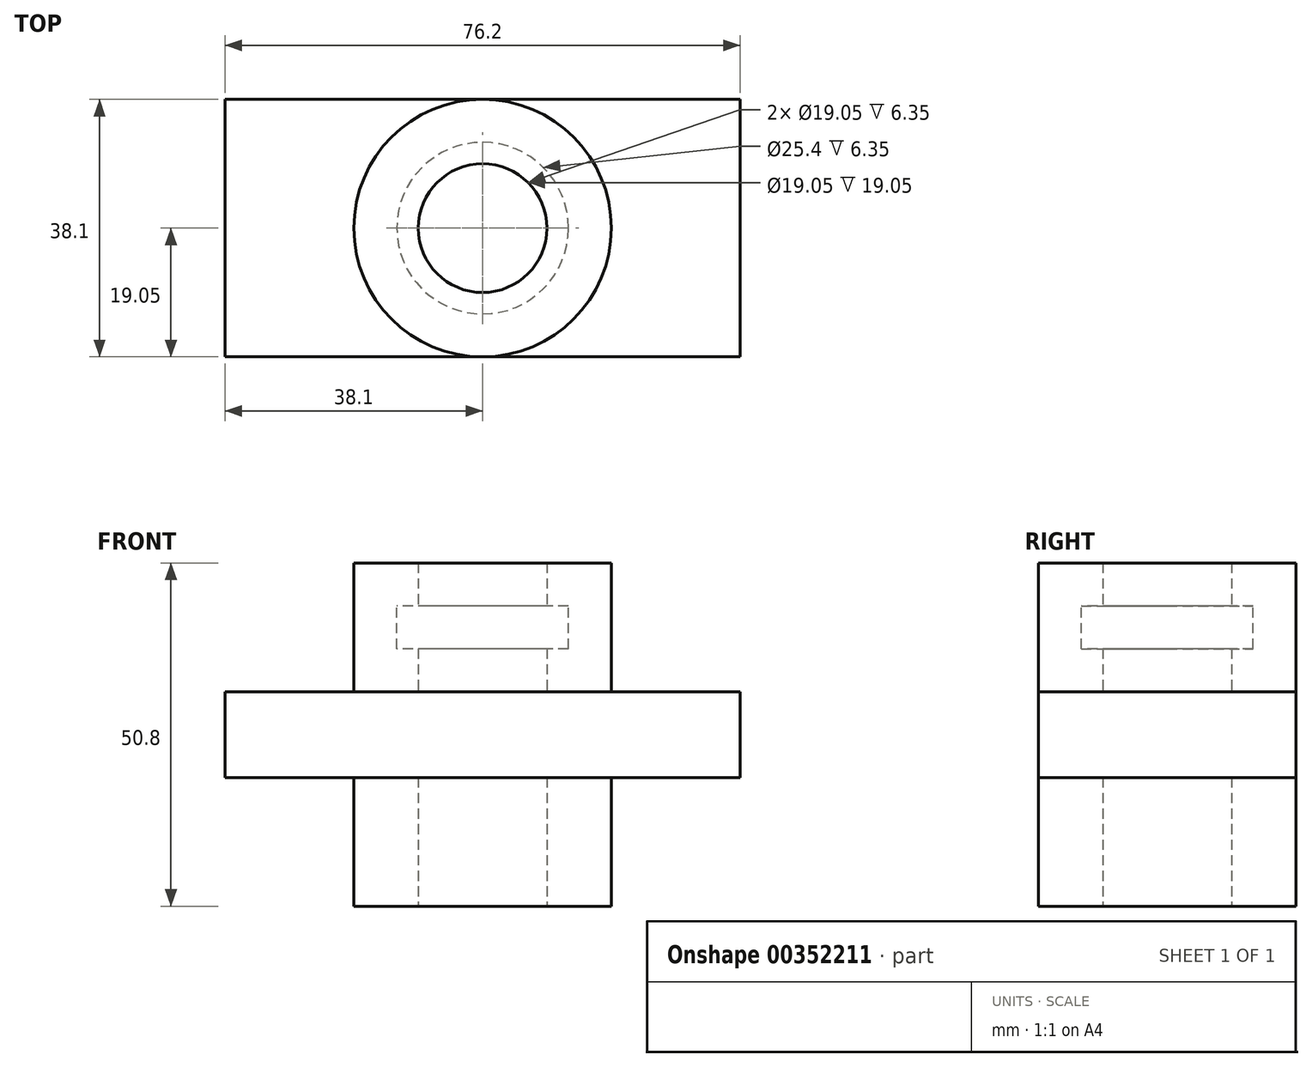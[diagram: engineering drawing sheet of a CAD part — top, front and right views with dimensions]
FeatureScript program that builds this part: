
annotation { "Feature Type Name" : "Feature", "Feature Type Description" : "" }
export const myFeature = defineFeature(function(context is Context, id is Id, definition is map)
    precondition{}
    {
        {
            var Q0;
            Q0=qCreatedBy(makeId("Top.planeOp"),FACE);
            var sketch = newSketch(context, id + "F0", { "sketchPlane" : qUnion([Q0])});
            skCircle(sketch, "E0", {"center": v(0, 0) * mm, "radius": 19.05 * mm});
            skCircle(sketch, "E1", {"center": v(0, 0) * mm, "radius": 9.53 * mm});
            skSolve(sketch);
        }
        {
            var Q0;
            Q0 = qSketchRegion(id + "F0", true);
            extrude(context, id + "F1", {"entities" : qUnion([Q0]), "endBound" : BoundingType.SYMMETRIC, "depth" : 50.8 * mm});
        }
        {
            var Q0;
            Q0=makeQuery(id+"F1.opExtrude","CAP_FACE",FACE,{"disambiguationData":[OSD([sQuery(id+"F0.wireOp",EDGE,"E0"),sQuery(id+"F0.wireOp",EDGE,"E1")])],"isStart":false});
            var sketch = newSketch(context, id + "F2", { "sketchPlane" : qUnion([Q0])});
            skCircle(sketch, "E2", {"center": v(0, 0) * mm, "radius": 12.7 * mm});
            skSolve(sketch);
        }
        {
            var Q0;
            Q0 = qSketchRegion(id + "F2", true);
            extrude(context, id + "F3", {"entities" : qUnion([Q0]), "operationType" : NewBodyOperationType.REMOVE, "oppositeDirection" : true, "depth" : 12.7 * mm, "hasSecondDirection" : true, "secondDirectionOppositeDirection" : true, "secondDirectionDepth" : 6.35 * mm});
        }
        {
            var Q0;
            Q0=qCreatedBy(makeId("Top.planeOp"),FACE);
            var sketch = newSketch(context, id + "F4", { "sketchPlane" : qUnion([Q0])});
            skLineSegment(sketch, "E3", {"start": v(-38.1, 0) * mm, "end": v(-38.1, 19.05) * mm});
            skLineSegment(sketch, "E4", {"start": v(-38.1, 19.05) * mm, "end": v(38.1, 19.05) * mm});
            skLineSegment(sketch, "E5", {"start": v(38.1, 19.05) * mm, "end": v(38.1, 0) * mm});
            skLineSegment(sketch, "E6", {"start": v(-53, 0) * mm, "end": v(50.74, 0) * mm, "construction": true});
            skLineSegment(sketch, "E7.MirrorCS", {"start": v(-38.1, 0) * mm, "end": v(-38.1, -19.05) * mm});
            skLineSegment(sketch, "E8.MirrorCS", {"start": v(-38.1, -19.05) * mm, "end": v(38.1, -19.05) * mm});
            skLineSegment(sketch, "E9.MirrorCS", {"start": v(38.1, -19.05) * mm, "end": v(38.1, 0) * mm});
            skSolve(sketch);
        }
        {
            var Q0;
            Q0 = qSketchRegion(id + "F4", true);
            extrude(context, id + "F5", {"entities" : qUnion([Q0]), "operationType" : NewBodyOperationType.ADD, "endBound" : BoundingType.SYMMETRIC, "depth" : 12.7 * mm});
        }
    });
